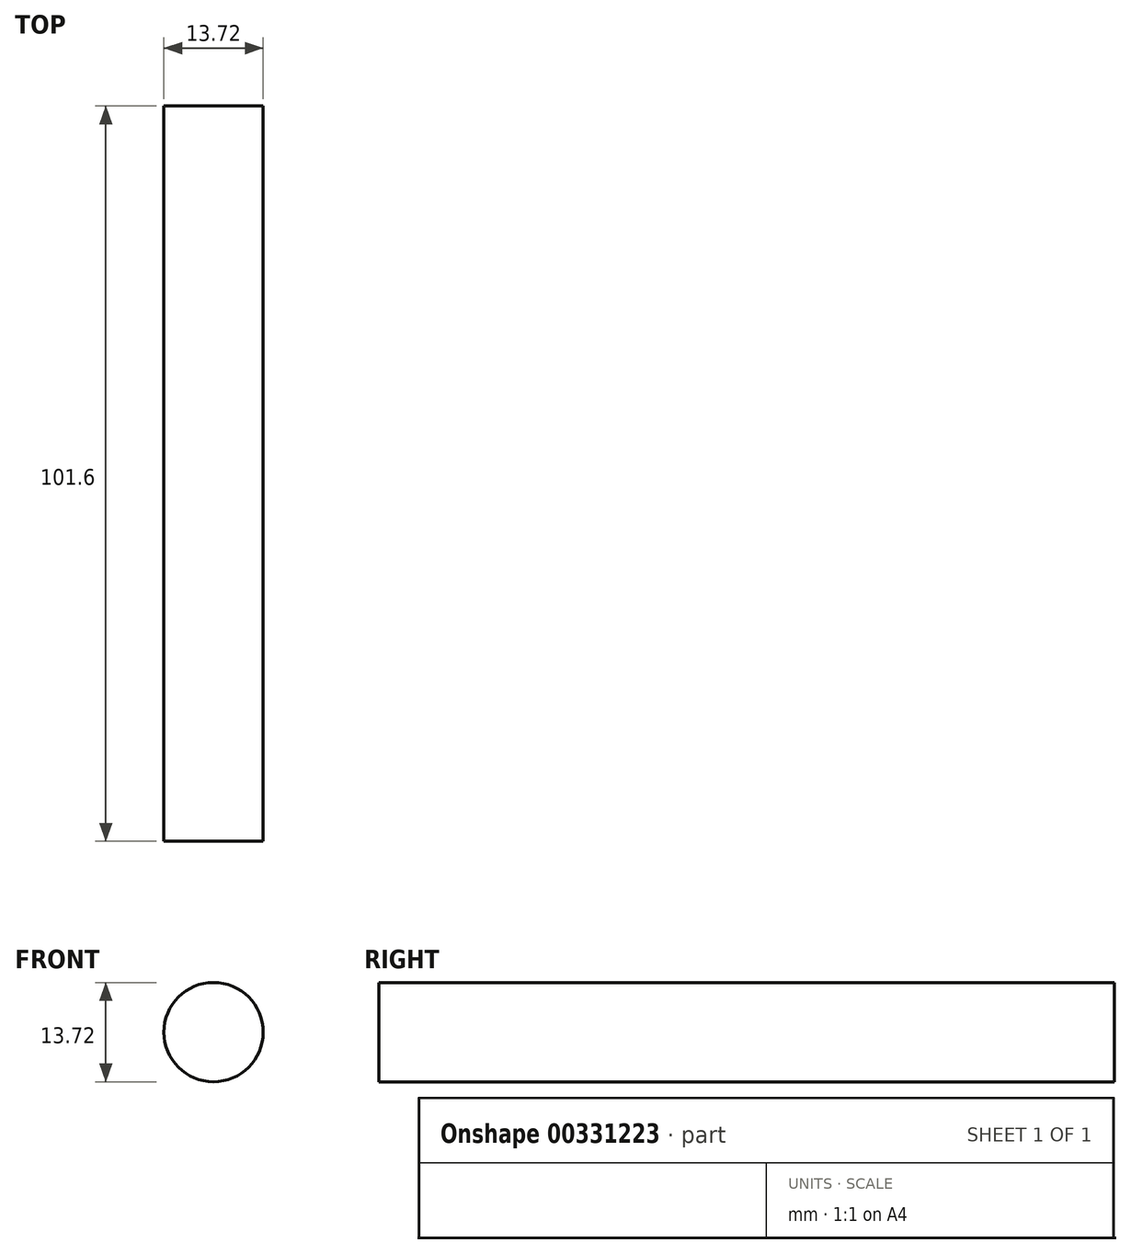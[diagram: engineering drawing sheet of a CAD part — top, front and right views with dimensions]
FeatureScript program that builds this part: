
annotation { "Feature Type Name" : "Feature", "Feature Type Description" : "" }
export const myFeature = defineFeature(function(context is Context, id is Id, definition is map)
    precondition{}
    {
        {
            var Q0;
            Q0=qCreatedBy(makeId("Front.planeOp"),FACE);
            var sketch = newSketch(context, id + "F0", { "sketchPlane" : qUnion([Q0])});
            skCircle(sketch, "E0", {"center": v(0, 0) * mm, "radius": 6.86 * mm});
            skSolve(sketch);
        }
        {
            var Q0;
            Q0 = qSketchRegion(id + "F0", true);
            extrude(context, id + "F1", {"entities" : qUnion([Q0]), "depth" : 101.6 * mm});
        }
    });
